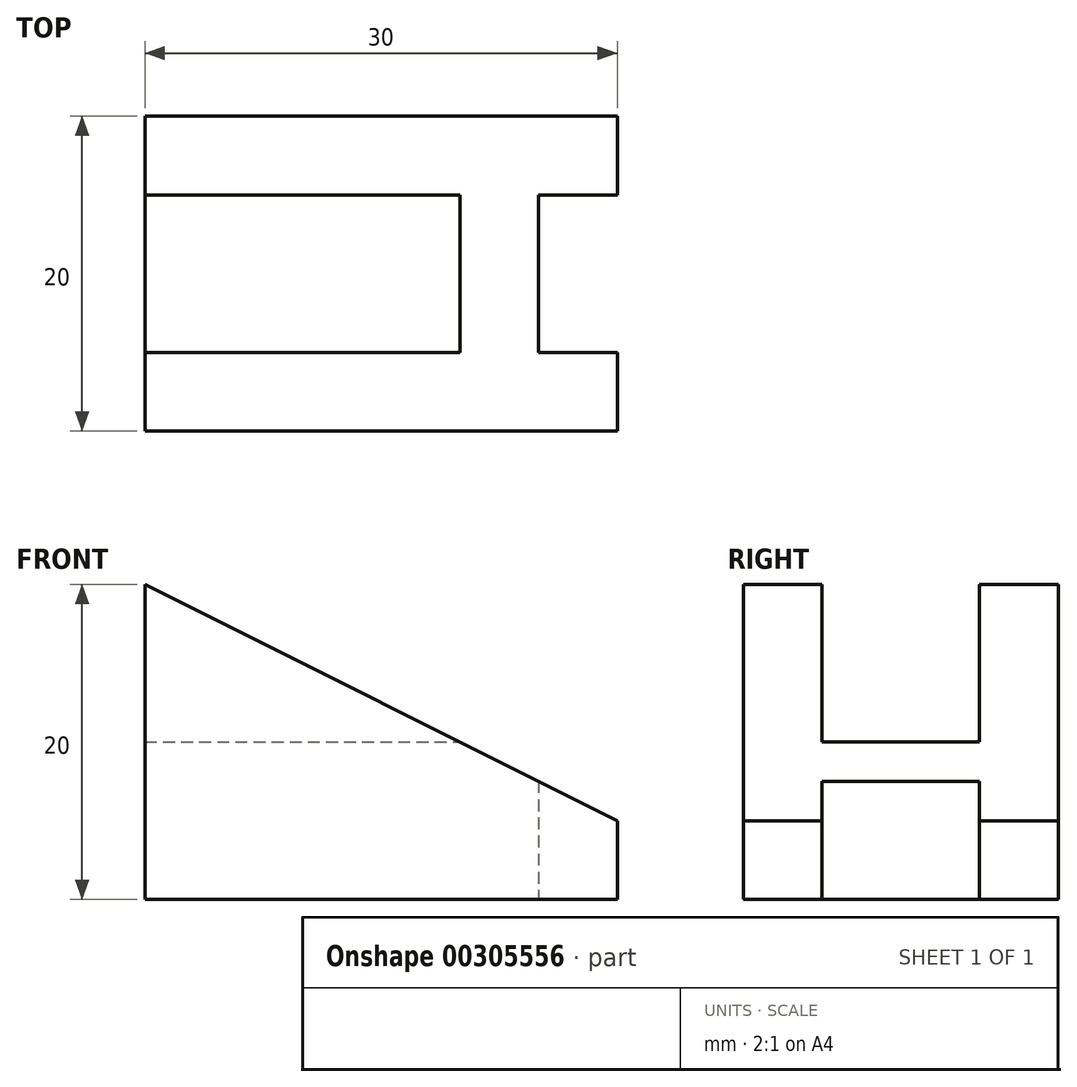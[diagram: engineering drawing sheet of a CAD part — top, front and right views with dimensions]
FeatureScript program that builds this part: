
annotation { "Feature Type Name" : "Feature", "Feature Type Description" : "" }
export const myFeature = defineFeature(function(context is Context, id is Id, definition is map)
    precondition{}
    {
        {
            var Q0;
            Q0=qCreatedBy(makeId("Front.planeOp"),FACE);
            var sketch = newSketch(context, id + "F0", { "sketchPlane" : qUnion([Q0])});
            skLineSegment(sketch, "E0", {"start": v(0, 0) * mm, "end": v(0, 20) * mm});
            skLineSegment(sketch, "E1", {"start": v(30, 0) * mm, "end": v(0, 0) * mm});
            skLineSegment(sketch, "E2", {"start": v(30, 0) * mm, "end": v(30, 5) * mm});
            skLineSegment(sketch, "E3", {"start": v(30, 5) * mm, "end": v(0, 20) * mm});
            skSolve(sketch);
        }
        {
            var Q0;
            Q0 = qSketchRegion(id + "F0", true);
            extrude(context, id + "F1", {"entities" : qUnion([Q0]), "endBound" : BoundingType.SYMMETRIC, "depth" : 20 * mm});
        }
        {
            var Q0;
            Q0=qCreatedBy(makeId("Front.planeOp"),FACE);
            var sketch = newSketch(context, id + "F2", { "sketchPlane" : qUnion([Q0])});
            skLineSegment(sketch, "E4", {"start": v(0, 20) * mm, "end": v(0, 10) * mm});
            skLineSegment(sketch, "E5", {"start": v(0, 10) * mm, "end": v(20, 10) * mm});
            skLineSegment(sketch, "E6", {"start": v(20, 10) * mm, "end": v(0, 20) * mm});
            skSolve(sketch);
        }
        {
            var Q0;
            Q0 = qSketchRegion(id + "F2", true);
            extrude(context, id + "F3", {"entities" : qUnion([Q0]), "operationType" : NewBodyOperationType.REMOVE, "oppositeDirection" : true, "depth" : 5 * mm, "hasSecondDirection" : true, "secondDirectionOppositeDirection" : false, "secondDirectionDepth" : 5 * mm});
        }
        {
            var Q0;
            Q0=makeQuery(id+"F1.opExtrude","SWEPT_FACE",FACE,{"disambiguationData":[OSD([sQuery(id+"F0.wireOp",EDGE,"E1")])]});
            var sketch = newSketch(context, id + "F4", { "sketchPlane" : qUnion([Q0])});
            skLineSegment(sketch, "E7", {"start": v(30, 5) * mm, "end": v(30, -5) * mm});
            skLineSegment(sketch, "E8", {"start": v(30, -5) * mm, "end": v(25, -5) * mm});
            skLineSegment(sketch, "E9", {"start": v(25, -5) * mm, "end": v(25, 5) * mm});
            skLineSegment(sketch, "E10", {"start": v(25, 5) * mm, "end": v(30, 5) * mm});
            skSolve(sketch);
        }
        {
            var Q0;
            Q0 = qSketchRegion(id + "F4", true);
            extrude(context, id + "F5", {"entities" : qUnion([Q0]), "operationType" : NewBodyOperationType.REMOVE, "endBound" : BoundingType.THROUGH_ALL, "oppositeDirection" : true, "depth" : 25 * mm});
        }
    });
